# Revit family: 63_UN_LightLine_Pacific LED Gen5 WT490C L1600 _Signify
name_source: partatom
category: Lighting Fixtures
units: mm (PartAtom-declared; Revit-internal decimal feet)

## family parameters
Always vertical = Yes
Cut with Voids When Loaded = Yes
Light Source = No
OmniClass Number = 23.80.70.11.14.11
OmniClass Title = Downlights
Part Type = Normal
Room Calculation Point = Yes
Round Connector Dimension = Use Diameter
Shared = No
Work Plane-Based = No

## types (1)
- Type Catalog
    Apparent Load = 19 VA
    Assembly Code = 63.0
    Description = IK08 - IP66
    Housing_Material = Laminate, White
    IfcExportAs = IfcLightFixtureType
    IfcExportType = USERDEFINED
    Lamp = LED
    Length = 1601 mm
    Light Source = WT490C L1600 - Lightsource : WT490C LED35S_830 NB-HRO PSD L1600
    Luminous Flux (lm) = 23 lm
    Manufacturer = Signify
    Model = Pacific LED Gen5 WT490C L1600
    Type Comments = WT490C L1600
    URL = https://www.signify.com
    Voltage = 230 V
    Wattage Comments = 19 W

## geometry (parser evidence)
native form markers: Sweep x19
no freeform markers — native parametric forms only
